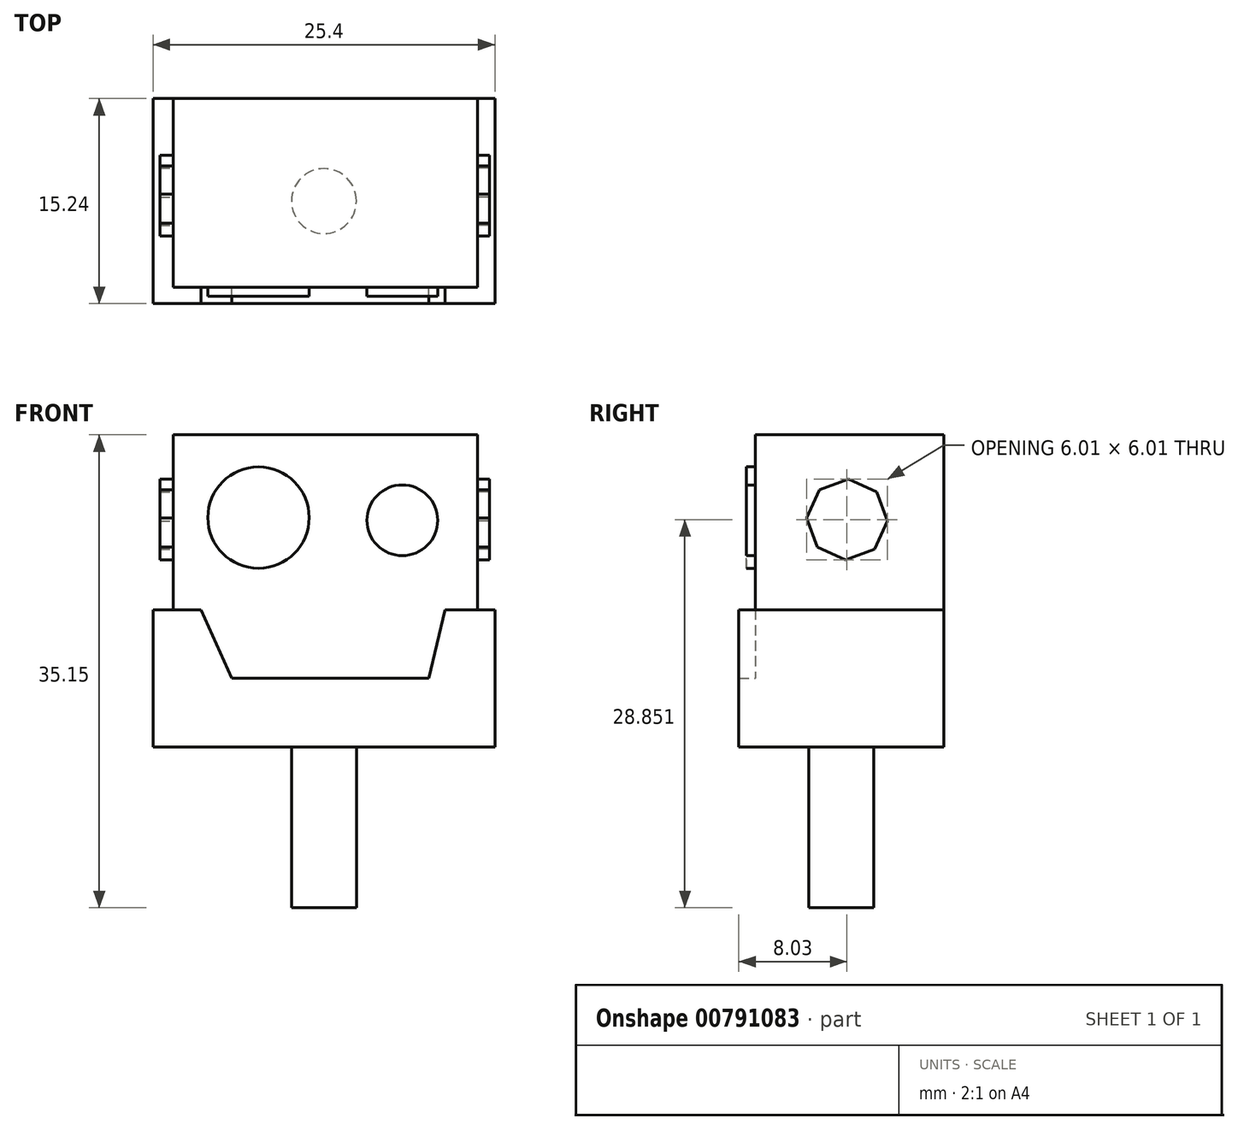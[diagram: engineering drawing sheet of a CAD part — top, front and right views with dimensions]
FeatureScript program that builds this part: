
annotation { "Feature Type Name" : "Feature", "Feature Type Description" : "" }
export const myFeature = defineFeature(function(context is Context, id is Id, definition is map)
    precondition{}
    {
        {
            var Q0;
            Q0=qCreatedBy(makeId("Front.planeOp"),FACE);
            var sketch = newSketch(context, id + "F0", { "sketchPlane" : qUnion([Q0])});
            skLineSegment(sketch, "E0", {"start": v(0, 0) * mm, "end": v(0, -10.21) * mm});
            skLineSegment(sketch, "E1", {"start": v(0, -10.21) * mm, "end": v(25.4, -10.21) * mm});
            skLineSegment(sketch, "E2", {"start": v(25.4, -10.21) * mm, "end": v(25.4, 0) * mm});
            skLineSegment(sketch, "E3", {"start": v(25.4, 0) * mm, "end": v(21.69, 0) * mm});
            skLineSegment(sketch, "E4", {"start": v(21.69, 0) * mm, "end": v(20.48, -5.08) * mm});
            skLineSegment(sketch, "E5", {"start": v(20.48, -5.08) * mm, "end": v(5.84, -5.08) * mm});
            skLineSegment(sketch, "E6", {"start": v(5.84, -5.08) * mm, "end": v(3.55, 0) * mm});
            skLineSegment(sketch, "E7", {"start": v(3.55, 0) * mm, "end": v(0, 0) * mm});
            skSolve(sketch);
        }
        {
            var Q0;
            Q0=makeQuery(id+"F0.imprint","IMPRINT",FACE,{"disambiguationData":[TD([[makeQuery(id+"F0.imprint","IMPRINT",EDGE,{"derivedFrom":sQuery(id+"F0.wireOp",EDGE,"E0")}),1.0]])]});
            extrude(context, id + "F1", {"entities" : qUnion([Q0]), "depth" : 15.24 * mm, "offsetDistance" : 25.4 * mm});
        }
        {
            var Q0;
            Q0=qCreatedBy(makeId("Front.planeOp"),FACE);
            var sketch = newSketch(context, id + "F2", { "sketchPlane" : qUnion([Q0])});
            skLineSegment(sketch, "E8.bottom", {"start": v(1.5, -6) * mm, "end": v(24.12, -6) * mm});
            skLineSegment(sketch, "E8.top", {"start": v(1.5, 13) * mm, "end": v(24.12, 13) * mm});
            skLineSegment(sketch, "E8.left", {"start": v(1.5, -6) * mm, "end": v(1.5, 13) * mm});
            skLineSegment(sketch, "E8.right", {"start": v(24.12, -6) * mm, "end": v(24.12, 13) * mm});
            skSolve(sketch);
        }
        {
            var Q0;
            Q0=makeQuery(id+"F2.imprint","IMPRINT",FACE,{"disambiguationData":[TD([[makeQuery(id+"F2.imprint","IMPRINT",EDGE,{"derivedFrom":sQuery(id+"F2.wireOp",EDGE,"E8.bottom")}),1.0]])]});
            extrude(context, id + "F3", {"entities" : qUnion([Q0]), "operationType" : NewBodyOperationType.ADD, "depth" : 14.02 * mm, "offsetDistance" : 25.4 * mm});
        }
        {
            var Q0;
            Q0=makeQuery(id+"F3.opExtrude","SWEPT_FACE",FACE,{"disambiguationData":[OSD([sQuery(id+"F2.wireOp",EDGE,"E8.right")])]});
            var sketch = newSketch(context, id + "F4", { "sketchPlane" : qUnion([Q0])});
            skCircle(sketch, "E9.cCircle", {"center": v(-7.2, 6.7) * mm, "radius": 2.78 * mm, "construction": true});
            skLineSegment(sketch, "E9.0", {"start": v(-9.26, 8.9) * mm, "end": v(-7.1, 9.7) * mm});
            skLineSegment(sketch, "E9.1", {"start": v(-7.1, 9.7) * mm, "end": v(-5, 8.75) * mm});
            skLineSegment(sketch, "E9.2", {"start": v(-5, 8.75) * mm, "end": v(-4.2, 6.6) * mm});
            skLineSegment(sketch, "E9.3", {"start": v(-4.2, 6.6) * mm, "end": v(-5.16, 4.5) * mm});
            skLineSegment(sketch, "E9.4", {"start": v(-5.16, 4.5) * mm, "end": v(-7.32, 3.7) * mm});
            skLineSegment(sketch, "E9.5", {"start": v(-7.32, 3.7) * mm, "end": v(-9.41, 4.66) * mm});
            skLineSegment(sketch, "E9.6", {"start": v(-9.41, 4.66) * mm, "end": v(-10.21, 6.81) * mm});
            skLineSegment(sketch, "E9.7", {"start": v(-10.21, 6.81) * mm, "end": v(-9.26, 8.9) * mm});
            skPoint(sketch, "E9.0.midPoint", {"position": v(-8.18, 9.3) * mm});
            skSolve(sketch);
        }
        {
            var Q0;
            Q0=makeQuery(id+"F4.imprint","IMPRINT",FACE,{"disambiguationData":[TD([[makeQuery(id+"F4.imprint","IMPRINT",EDGE,{"derivedFrom":sQuery(id+"F4.wireOp",EDGE,"E9.0")}),-1.0]])]});
            extrude(context, id + "F5", {"entities" : qUnion([Q0]), "operationType" : NewBodyOperationType.ADD, "oppositeDirection" : true, "depth" : 23.62 * mm, "offsetDistance" : 25.4 * mm});
        }
        {
            var Q0;
            Q0 = qSketchRegion(id + "F4", true);
            extrude(context, id + "F6", {"entities" : qUnion([Q0]), "operationType" : NewBodyOperationType.ADD, "depth" : 0.86 * mm, "offsetDistance" : 25.4 * mm});
        }
        {
            var Q0;
            Q0=makeQuery(id+"F3.opExtrude","CAP_FACE",FACE,{"disambiguationData":[OSD([sQuery(id+"F2.wireOp",EDGE,"E8.bottom"),sQuery(id+"F2.wireOp",EDGE,"E8.top"),sQuery(id+"F2.wireOp",EDGE,"E8.left"),sQuery(id+"F2.wireOp",EDGE,"E8.right")])],"isStart":false});
            var sketch = newSketch(context, id + "F7", { "sketchPlane" : qUnion([Q0])});
            skCircle(sketch, "E10", {"center": v(7.83, 6.85) * mm, "radius": 3.77 * mm});
            skCircle(sketch, "E11", {"center": v(18.52, 6.64) * mm, "radius": 2.63 * mm});
            skSolve(sketch);
        }
        {
            var Q0;
            Q0=makeQuery(id+"F7.imprint","IMPRINT",FACE,{"disambiguationData":[TD([[makeQuery(id+"F7.imprint","IMPRINT",EDGE,{"derivedFrom":sQuery(id+"F7.wireOp",EDGE,"E10")}),1.0]])]});
            var Q1;
            Q1=makeQuery(id+"F7.imprint","IMPRINT",FACE,{"disambiguationData":[TD([[makeQuery(id+"F7.imprint","IMPRINT",EDGE,{"derivedFrom":sQuery(id+"F7.wireOp",EDGE,"E11")}),1.0]])]});
            extrude(context, id + "F8", {"entities" : qUnion([Q0, Q1]), "operationType" : NewBodyOperationType.ADD, "depth" : 0.66 * mm, "offsetDistance" : 25.4 * mm});
        }
        {
            var Q0;
            Q0=makeQuery(id+"F1.opExtrude","SWEPT_FACE",FACE,{"disambiguationData":[OSD([sQuery(id+"F0.wireOp",EDGE,"E1")])]});
            var sketch = newSketch(context, id + "F9", { "sketchPlane" : qUnion([Q0])});
            skCircle(sketch, "E12", {"center": v(12.7, 7.62) * mm, "radius": 2.41 * mm});
            skPoint(sketch, "E12.centerSnap0", {"position": v(25.4, 7.62) * mm});
            skPoint(sketch, "E12.centerSnap1", {"position": v(12.7, 15.24) * mm});
            skSolve(sketch);
        }
        {
            var Q0;
            Q0=makeQuery(id+"F9.imprint","IMPRINT",FACE,{"disambiguationData":[TD([[makeQuery(id+"F9.imprint","IMPRINT",EDGE,{"derivedFrom":sQuery(id+"F9.wireOp",EDGE,"E12")}),1.0]])]});
            extrude(context, id + "F10", {"entities" : qUnion([Q0]), "operationType" : NewBodyOperationType.ADD, "depth" : 11.94 * mm, "offsetDistance" : 25.4 * mm});
        }
    });
